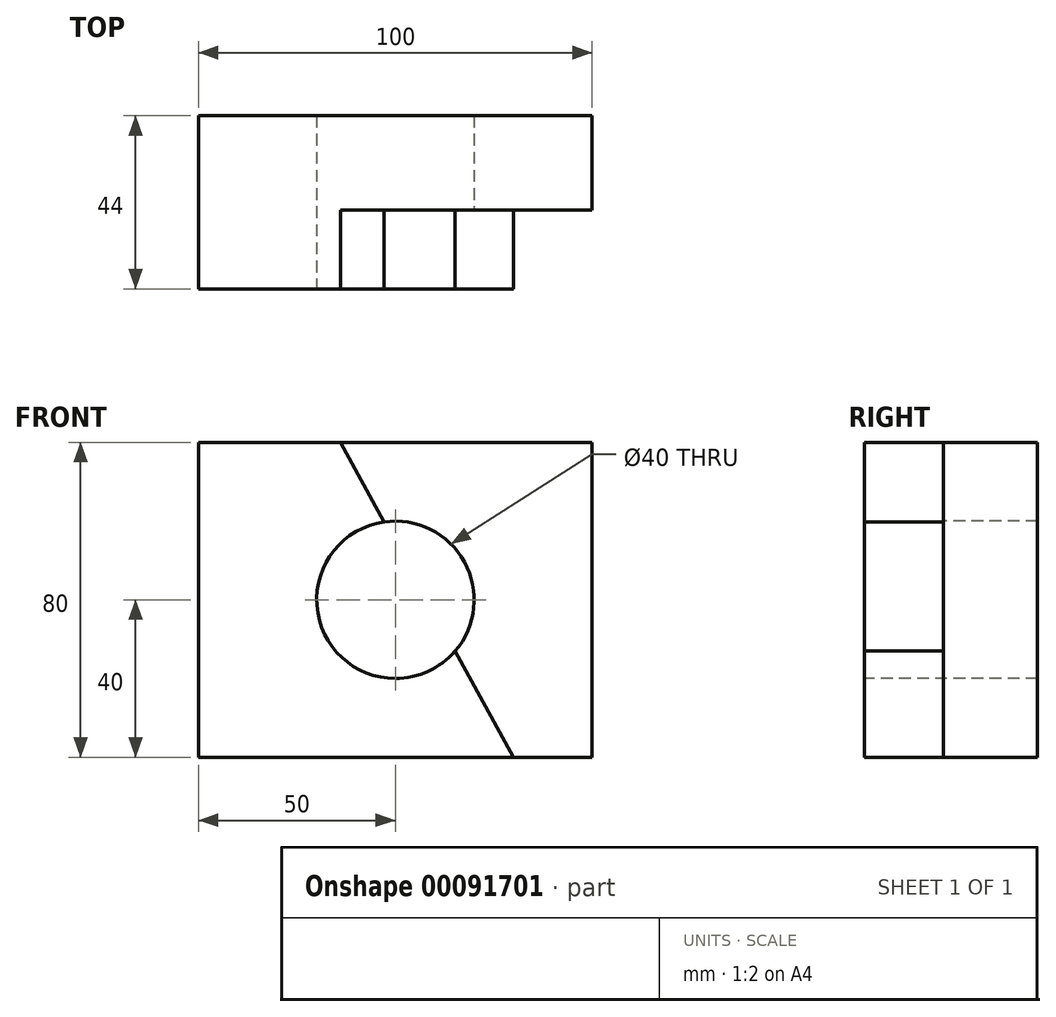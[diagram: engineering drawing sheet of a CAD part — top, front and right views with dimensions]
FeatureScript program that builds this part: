
annotation { "Feature Type Name" : "Feature", "Feature Type Description" : "" }
export const myFeature = defineFeature(function(context is Context, id is Id, definition is map)
    precondition{}
    {
        {
            var Q0;
            Q0=qCreatedBy(makeId("Front.planeOp"),FACE);
            var sketch = newSketch(context, id + "F0", { "sketchPlane" : qUnion([Q0])});
            skLineSegment(sketch, "E0.bottom", {"start": v(-50, 40) * mm, "end": v(50, 40) * mm});
            skLineSegment(sketch, "E0.top", {"start": v(-50, -40) * mm, "end": v(50, -40) * mm});
            skLineSegment(sketch, "E0.left", {"start": v(-50, 40) * mm, "end": v(-50, -40) * mm});
            skLineSegment(sketch, "E0.right", {"start": v(50, 40) * mm, "end": v(50, -40) * mm});
            skPoint(sketch, "E0.middle", {"position": v(0, 0) * mm});
            skSolve(sketch);
        }
        {
            var Q0;
            Q0=makeQuery(id+"F0.imprint","IMPRINT",FACE,{"disambiguationData":[TD([[makeQuery(id+"F0.imprint","IMPRINT",EDGE,{"derivedFrom":sQuery(id+"F0.wireOp",EDGE,"E0.bottom")}),-1.0]])]});
            extrude(context, id + "F1", {"entities" : qUnion([Q0]), "depth" : 44 * mm});
        }
        {
            var Q0;
            Q0=makeQuery(id+"F1.opExtrude","CAP_FACE",FACE,{"disambiguationData":[OSD([sQuery(id+"F0.wireOp",EDGE,"E0.bottom"),sQuery(id+"F0.wireOp",EDGE,"E0.top"),sQuery(id+"F0.wireOp",EDGE,"E0.left"),sQuery(id+"F0.wireOp",EDGE,"E0.right")])],"isStart":false});
            var sketch = newSketch(context, id + "F2", { "sketchPlane" : qUnion([Q0])});
            skCircle(sketch, "E1", {"center": v(0, 0) * mm, "radius": 20 * mm});
            skSolve(sketch);
        }
        {
            var Q0;
            Q0 = qSketchRegion(id + "F2", true);
            extrude(context, id + "F3", {"entities" : qUnion([Q0]), "operationType" : NewBodyOperationType.REMOVE, "oppositeDirection" : true, "depth" : 50 * mm});
        }
        {
            var Q0;
            Q0=makeQuery(id+"F1.opExtrude","CAP_FACE",FACE,{"disambiguationData":[OSD([sQuery(id+"F0.wireOp",EDGE,"E0.bottom"),sQuery(id+"F0.wireOp",EDGE,"E0.top"),sQuery(id+"F0.wireOp",EDGE,"E0.left"),sQuery(id+"F0.wireOp",EDGE,"E0.right")])],"isStart":false});
            var sketch = newSketch(context, id + "F4", { "sketchPlane" : qUnion([Q0])});
            skLineSegment(sketch, "E2", {"start": v(-50, 40) * mm, "end": v(-14, 40) * mm});
            skLineSegment(sketch, "E3", {"start": v(30, -40) * mm, "end": v(-50, -40) * mm});
            skLineSegment(sketch, "E4", {"start": v(-50, -40) * mm, "end": v(-50, 40) * mm});
            skLineSegment(sketch, "E5", {"start": v(-14, 40) * mm, "end": v(30, -40) * mm});
            skSolve(sketch);
        }
        {
            var Q0;
            {var subQ0=makeQuery(id+"F1.opExtrude","CAP_EDGE",EDGE,{"disambiguationData":[OSD([sQuery(id+"F0.wireOp",EDGE,"E0.right")])],"isStart":false});Q0=makeQuery(id+"F4.imprint","IMPRINT",FACE,{"disambiguationData":[TD([[makeQuery(id+"F4.imprint","IMPRINT",EDGE,{"derivedFrom":subQ0}),-1.0]])]});}
            extrude(context, id + "F5", {"entities" : qUnion([Q0]), "operationType" : NewBodyOperationType.REMOVE, "oppositeDirection" : true, "depth" : 20 * mm});
        }
    });
